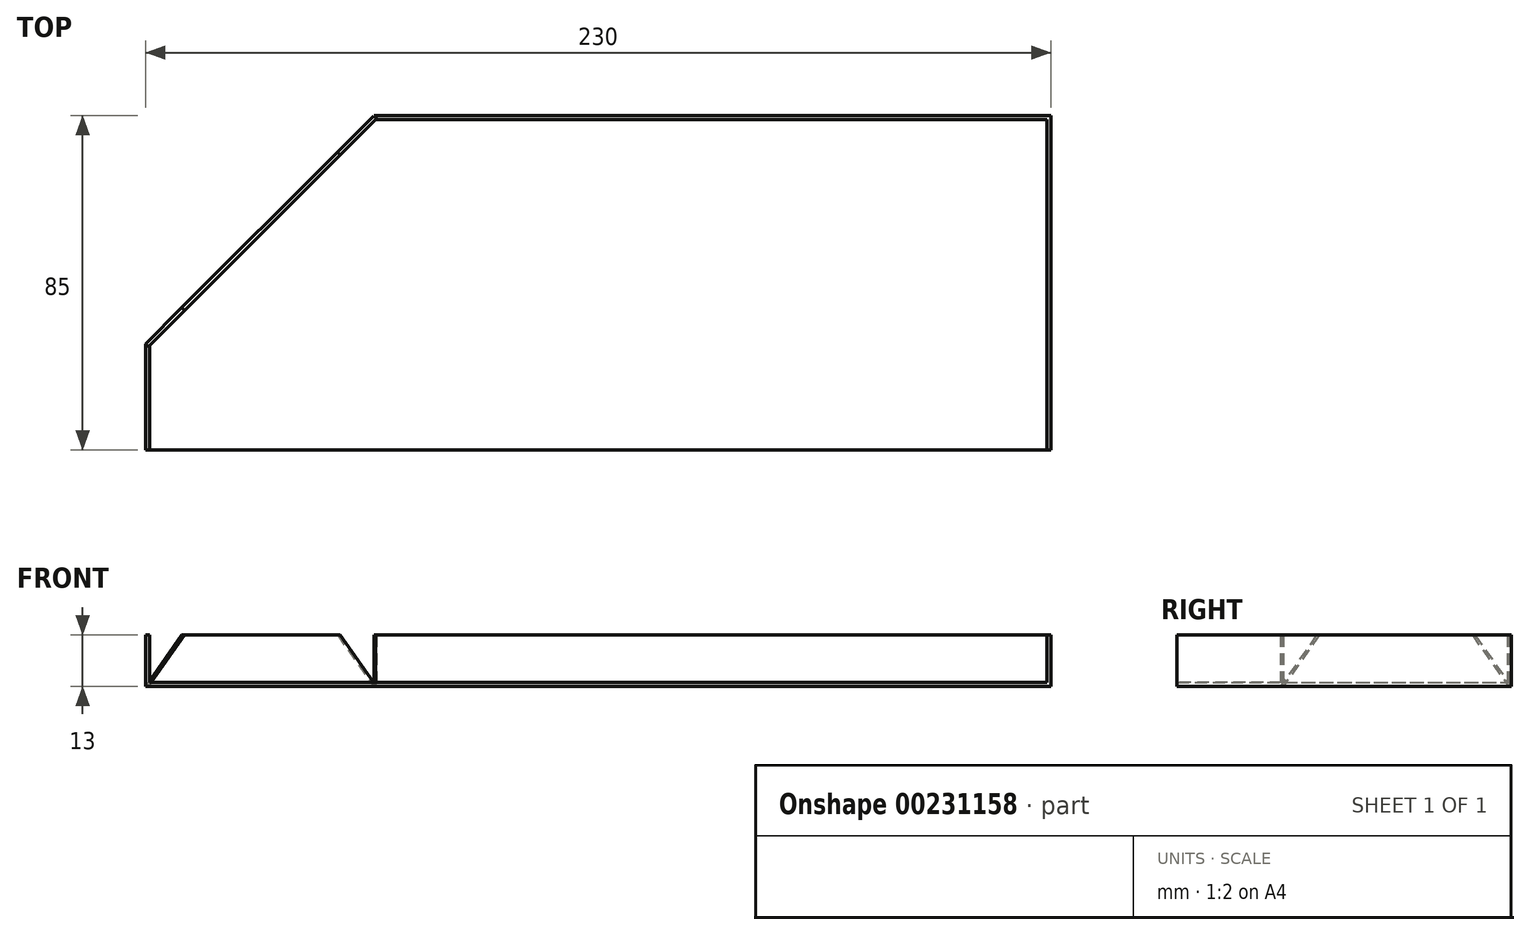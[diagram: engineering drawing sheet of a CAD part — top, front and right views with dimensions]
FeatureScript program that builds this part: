
annotation { "Feature Type Name" : "Feature", "Feature Type Description" : "" }
export const myFeature = defineFeature(function(context is Context, id is Id, definition is map)
    precondition{}
    {
        {
            var Q0;
            Q0=qCreatedBy(makeId("Top.planeOp"),FACE);
            var sketch = newSketch(context, id + "F0", { "sketchPlane" : qUnion([Q0])});
            skLineSegment(sketch, "E0.bottom", {"start": v(115, -42.5) * mm, "end": v(-115, -42.5) * mm});
            skLineSegment(sketch, "E0.top", {"start": v(115, 42.5) * mm, "end": v(-57, 42.5) * mm});
            skLineSegment(sketch, "E0.left", {"start": v(115, -42.5) * mm, "end": v(115, 42.5) * mm});
            skLineSegment(sketch, "E0.right", {"start": v(-115, -42.5) * mm, "end": v(-115, -15.5) * mm});
            skPoint(sketch, "E0.middle", {"position": v(0, 0) * mm});
            skLineSegment(sketch, "E1", {"start": v(-115, -15.5) * mm, "end": v(-57, 42.5) * mm});
            skPoint(sketch, "E2.orphan", {"position": v(-115, 42.5) * mm});
            skSolve(sketch);
        }
        {
            var Q0;
            Q0=qSketchRegion(id+"F0",true);
            extrude(context, id + "F1", {"entities" : qUnion([Q0]), "depth" : 1 * mm});
        }
        {
            var Q0;
            Q0=makeQuery(id+"F1.opExtrude","CAP_FACE",FACE,{"disambiguationData":[OSD([sQuery(id+"F0.wireOp",EDGE,"E0.bottom"),sQuery(id+"F0.wireOp",EDGE,"E0.top"),sQuery(id+"F0.wireOp",EDGE,"E0.left"),sQuery(id+"F0.wireOp",EDGE,"E0.right"),sQuery(id+"F0.wireOp",EDGE,"E1")])],"isStart":false});
            var sketch = newSketch(context, id + "F2", { "sketchPlane" : qUnion([Q0])});
            skLineSegment(sketch, "E3", {"start": v(-115, -42.5) * mm, "end": v(-115, -15.5) * mm});
            skLineSegment(sketch, "E4", {"start": v(-115, -15.5) * mm, "end": v(-57, 42.5) * mm});
            skLineSegment(sketch, "E5", {"start": v(-57, 42.5) * mm, "end": v(115, 42.5) * mm});
            skLineSegment(sketch, "E6", {"start": v(115, 42.5) * mm, "end": v(115, -42.5) * mm});
            skLineSegment(sketch, "E7", {"start": v(115, -42.5) * mm, "end": v(114, -42.5) * mm});
            skLineSegment(sketch, "E8", {"start": v(114, -42.5) * mm, "end": v(114, 41.5) * mm});
            skLineSegment(sketch, "E9", {"start": v(114, 41.5) * mm, "end": v(-56.59, 41.5) * mm});
            skLineSegment(sketch, "E10", {"start": v(-114, -15.91) * mm, "end": v(-114, -42.5) * mm});
            skLineSegment(sketch, "E11", {"start": v(-114, -42.5) * mm, "end": v(-115, -42.5) * mm});
            skLineSegment(sketch, "E12", {"start": v(-114, -15.91) * mm, "end": v(-56.59, 41.5) * mm});
            skSolve(sketch);
        }
        {
            var Q0;
            Q0=qSketchRegion(id+"F2",true);
            extrude(context, id + "F3", {"entities" : qUnion([Q0]), "operationType" : NewBodyOperationType.ADD, "depth" : 12 * mm});
        }
        {
            var Q0;
            Q0=makeQuery(id+"F3.boolean.opBoolean","MERGE",FACE,{"derivedFrom":[makeQuery(id+"F1.opExtrude","SWEPT_FACE",FACE,{"disambiguationData":[OSD([sQuery(id+"F0.wireOp",EDGE,"E1")])]}),makeQuery(id+"F3.opExtrude","SWEPT_FACE",FACE,{"disambiguationData":[OSD([sQuery(id+"F2.wireOp",EDGE,"E4")])]})]});
            var sketch = newSketch(context, id + "F4", { "sketchPlane" : qUnion([Q0])});
            skLineSegment(sketch, "E13", {"start": v(92.28, 0) * mm, "end": v(92.28, 13) * mm});
            skLineSegment(sketch, "E14", {"start": v(92.28, 13) * mm, "end": v(79.27, 13) * mm});
            skLineSegment(sketch, "E15", {"start": v(79.27, 13) * mm, "end": v(92.27, 0) * mm});
            skLineSegment(sketch, "E16", {"start": v(92.27, 0) * mm, "end": v(92.28, 0) * mm});
            skLineSegment(sketch, "E17", {"start": v(10.25, 13) * mm, "end": v(23.35, 13) * mm});
            skLineSegment(sketch, "E18", {"start": v(23.35, 13) * mm, "end": v(10.35, 0) * mm});
            skLineSegment(sketch, "E19", {"start": v(10.35, 0) * mm, "end": v(10.25, 0) * mm});
            skLineSegment(sketch, "E20", {"start": v(10.25, 0) * mm, "end": v(10.25, 13) * mm});
            skSolve(sketch);
        }
        {
            var Q0;
            Q0=qSketchRegion(id+"F4",true);
            var Q1;
            Q1=makeQuery(id+"F3.opExtrude","SWEPT_FACE",FACE,{"disambiguationData":[OSD([sQuery(id+"F2.wireOp",EDGE,"E12")])]});
            extrude(context, id + "F5", {"entities" : qUnion([Q0]), "operationType" : NewBodyOperationType.REMOVE, "oppositeDirection" : true, "endBoundEntityFace" : qUnion([Q1]), "depth" : 1 * mm});
        }
    });
